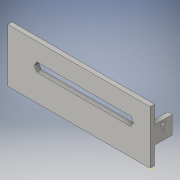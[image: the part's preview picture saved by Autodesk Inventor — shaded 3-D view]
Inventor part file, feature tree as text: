
AUTODESK INVENTOR PART (.ipt)
format: ipt  version: 2016 (Build 200138000, 138)  size: 145,408 bytes
history: native  units: in
note: dims shown in document units (in); Inventor stores cm internally (conversion verified against a paired STEP export)
features: sketch x7, extrude x5
ambient origin geometry x8: Origin, YZ Plane, XZ Plane, XY Plane, X Axis, Y Axis, Z Axis, Center Point
bodies: Solid1 (feature_tree)
feature tree (12):
  extrude  "Extrusion1"  Depth=8.0in
  sketch  "Sketch2"  dims[d2=3.0in d3=0.0in d4=5.0in]
  sketch  "Sketch3"  dims[d5=0.5in d6=0.25in d7=0.0in]
  extrude  "Extrusion2"  Depth=3.0in
  sketch  "Sketch4"  dims[d8=0.25in d9=2.0in]
  extrude  "Extrusion3"  Depth=0.25in TaperAngle=0.0deg
  extrude  "Extrusion4"  Depth=2.0in
  extrude  "Extrusion5"  Depth=1.0in TaperAngle=0.0deg
  sketch  "Sketch1"  dims[d0=0.25in d1=8.0in]
  sketch  "Sketch5"  dims[d11=1.0in d12=1.0in d13=0.0in]
  sketch  "Sketch6"  dims[d14=0.25in]
  sketch  "Sketch7"  dims[d15=0.125in d16=0.5in d17=0.2in d18=0.25in d19=0.0in d20=0.5in d21=0.5in d22=0.25in d23=0.0in d24=1.0in d25=1.22in]
